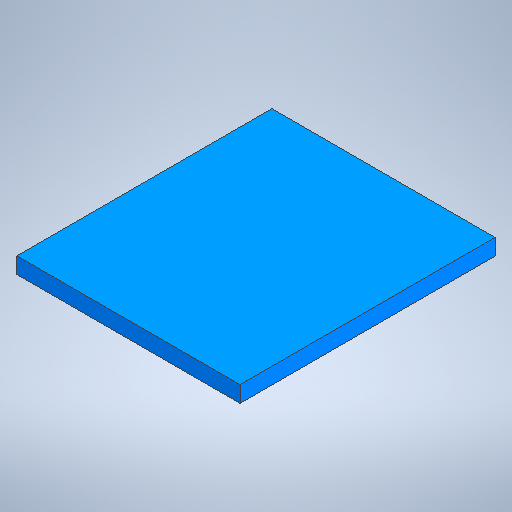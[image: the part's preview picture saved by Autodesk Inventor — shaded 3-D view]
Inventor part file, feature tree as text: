
AUTODESK INVENTOR PART (.ipt)
format: ipt  version: 2025.2 (Build 292293000, 293)  size: 208,384 bytes
history: native  units: mm
features: extrude x1, sketch x1
ambient origin geometry x8: Origin, YZ Plane, XZ Plane, XY Plane, X Axis, Y Axis, Z Axis, Center Point
bodies: Solid1 (feature_tree)
feature tree (2):
  extrude  "Extrusion1"  Depth=400.0mm
  sketch  "Sketch1"  dims[d0=350.0mm d1=400.0mm d2=25.4mm d3=0.0mm]
